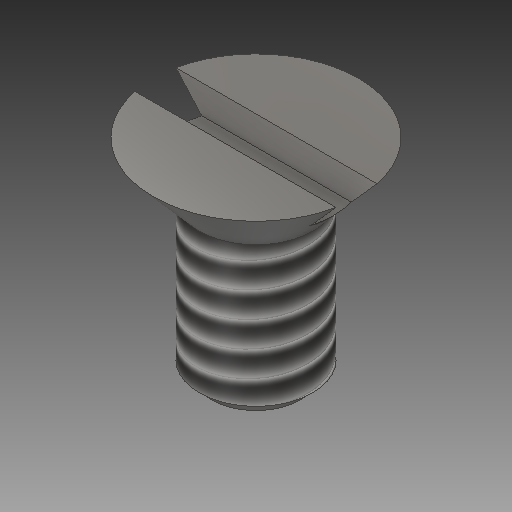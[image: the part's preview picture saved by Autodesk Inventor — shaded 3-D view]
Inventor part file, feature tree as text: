
AUTODESK INVENTOR PART (.ipt)
format: ipt  version: 2018 (Build 220112000, 112)  size: 163,328 bytes
history: native  units: in
note: dims shown in document units (in); Inventor stores cm internally (conversion verified against a paired STEP export)
features: sketch x2, revolve x1, extrude x1, chamfer x1, thread x1, projected_geometry x1
ambient origin geometry x8: Origin, YZ Plane, XZ Plane, XY Plane, X Axis, Y Axis, Z Axis, Center Point
bodies: Solid1 (feature_tree)
feature tree (7):
  revolve  "Revolution1"  [1 undecoded]
  extrude  "Extrusion1"  Depth=0.25in
  chamfer  "Chamfer1"  Angle=90.0deg  [1 undecoded]
  thread  "Thread1"  [1 undecoded]
  sketch  "Sketch1"  dims[d0=0.25in d1=0.138in]
  sketch  "Sketch2"  dims[d2=0.5635in d3=0.25in d4=90.0deg d5=0.05in d6=0.035in d7=1.0in d8=0.0in d9=0.015in d10=0.125in d11=45.0deg d12=1.0in d13=0.0in]
  projected_geometry  "Projected Loop1"
note: 3 required parameter values undecoded (feature->parameter linkage not recoverable at this tier; creation-order binding heuristic only, values carry confidence <= 0.55)